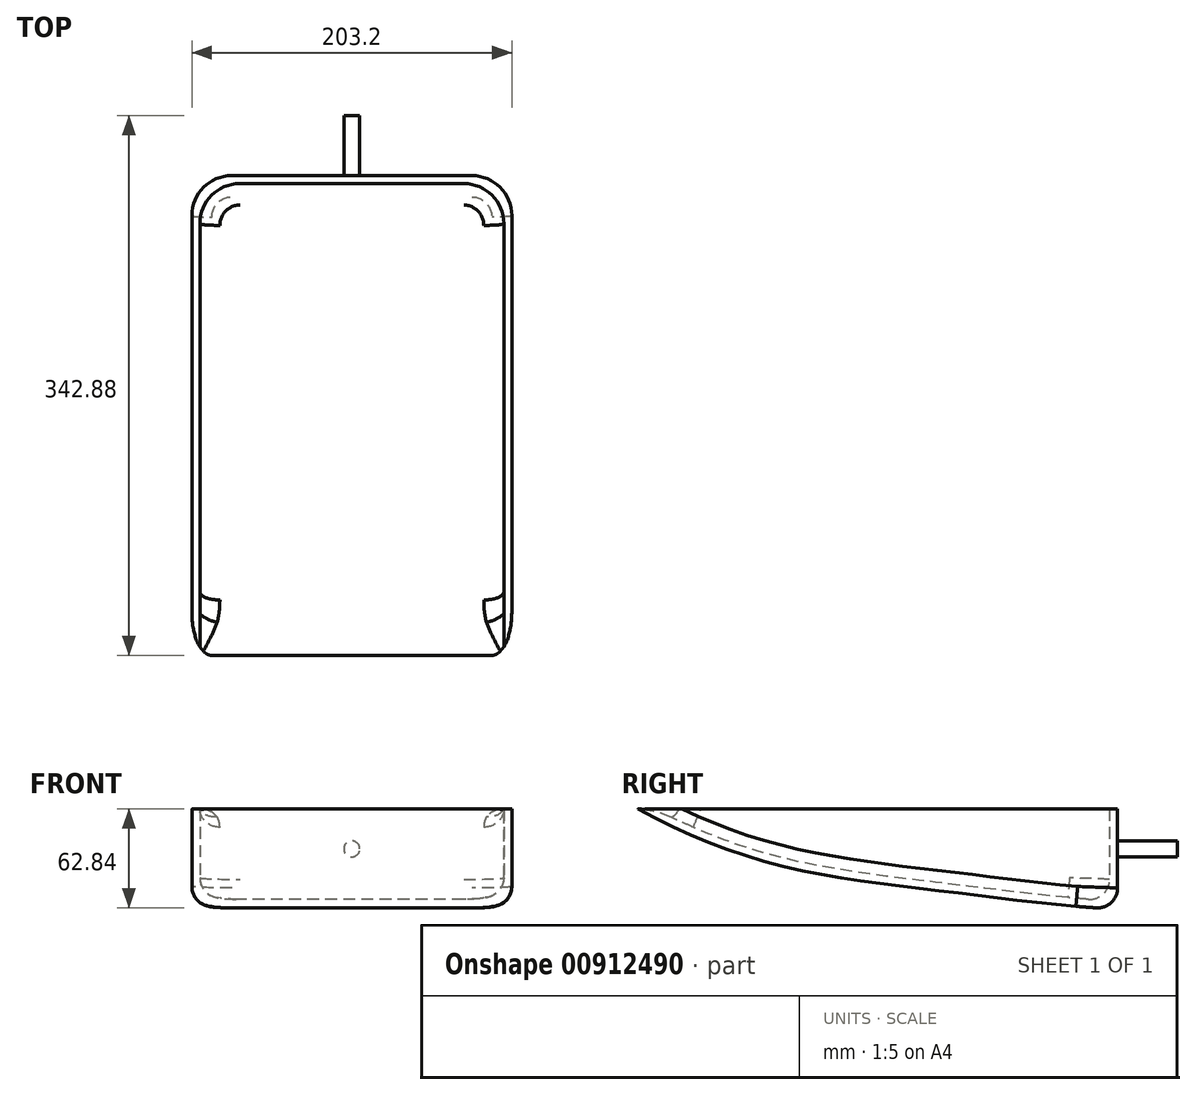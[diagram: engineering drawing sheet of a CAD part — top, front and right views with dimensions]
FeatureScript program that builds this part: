
annotation { "Feature Type Name" : "Feature", "Feature Type Description" : "" }
export const myFeature = defineFeature(function(context is Context, id is Id, definition is map)
    precondition{}
    {
        {
            var Q0;
            Q0=qCreatedBy(makeId("Right.planeOp"),FACE);
            var sketch = newSketch(context, id + "F0", { "sketchPlane" : qUnion([Q0])});
            skLineSegment(sketch, "E0", {"start": v(-153.93, 25.4) * mm, "end": v(150.87, 25.4) * mm});
            skLineSegment(sketch, "E1", {"start": v(150.87, 25.4) * mm, "end": v(150.87, -38.1) * mm});
            skFitSpline(sketch, "E2", {"points": [v(150.87, -38.1) * mm, v(48.07, -27.8) * mm, v(-62.6, -10.78) * mm, v(-153.93, 25.4) * mm], "startDerivative": vector(-306.13, 11.4) * mm, "endDerivative": vector(-268.95, 145.28) * mm});
            skLineSegment(sketch, "E3", {"start": v(131.63, 25.4) * mm, "end": v(131.63, 0) * mm, "construction": true});
            skSolve(sketch);
        }
        {
            var Q0;
            Q0=makeQuery(id+"F0.imprint","IMPRINT",FACE,{"disambiguationData":[TD([[makeQuery(id+"F0.imprint","IMPRINT",EDGE,{"derivedFrom":sQuery(id+"F0.wireOp",EDGE,"E0")}),-1.0]])]});
            extrude(context, id + "F1", {"entities" : qUnion([Q0]), "endBound" : BoundingType.SYMMETRIC, "depth" : 203.2 * mm, "offsetDistance" : 25.4 * mm});
        }
        {
            var Q0;
            Q0=makeQuery(id+"F1.opExtrude","SWEPT_FACE",FACE,{"disambiguationData":[OSD([sQuery(id+"F0.wireOp",EDGE,"E0")])]});
            shell(context, id + "F2", {"entities" : qUnion([Q0]), "thickness" : 5.08 * mm});
        }
        {
            var Q0;
            {var subQ0=sQuery(id+"F0.wireOp",EDGE,"E1");Q0=makeQuery(id+"F2.opShell","OFFSET_EDGE",EDGE,{"disambiguationData":[OSD([subQ0]),TDD([makeQuery(id+"F1.opExtrude","CAP_EDGE",EDGE,{"disambiguationData":[OSD([subQ0])],"isStart":false})])]});}
            fillet(context, id + "F3", {"entities" : qUnion([Q0]), "radius" : 25.4 * mm, "tangentPropagation" : true, "allowEdgeOverflow" : false});
        }
        {
            var Q0;
            {var subQ0=sQuery(id+"F0.wireOp",EDGE,"E1");Q0=makeQuery(id+"F2.opShell","OFFSET_EDGE",EDGE,{"disambiguationData":[OSD([subQ0]),TDD([makeQuery(id+"F1.opExtrude","CAP_EDGE",EDGE,{"disambiguationData":[OSD([subQ0])],"isStart":true})])]});}
            fillet(context, id + "F4", {"entities" : qUnion([Q0]), "radius" : 25.4 * mm, "tangentPropagation" : true, "allowEdgeOverflow" : false});
        }
        {
            var Q0;
            Q0=makeQuery(id+"F2.opShell","OFFSET_EDGE",EDGE,{"disambiguationData":[OSD([sQuery(id+"F0.wireOp",EDGE,"E0"),sQuery(id+"F0.wireOp",EDGE,"E2")])]});
            fillet(context, id + "F5", {"entities" : qUnion([Q0]), "radius" : 50.8 * mm, "tangentPropagation" : true, "allowEdgeOverflow" : false});
        }
        {
            var Q0;
            Q0=makeQuery(id+"F1.opExtrude","CAP_EDGE",EDGE,{"disambiguationData":[OSD([sQuery(id+"F0.wireOp",EDGE,"E1")])],"isStart":false});
            var Q1;
            Q1=makeQuery(id+"F1.opExtrude","CAP_EDGE",EDGE,{"disambiguationData":[OSD([sQuery(id+"F0.wireOp",EDGE,"E1")])],"isStart":true});
            fillet(context, id + "F6", {"entities" : qUnion([Q0, Q1]), "radius" : 25.4 * mm, "tangentPropagation" : true, "allowEdgeOverflow" : false});
        }
        {
            var Q0;
            Q0=makeQuery(id+"F6.opFillet","BLEND_EDGE",EDGE,{"blendedFrom":[makeQuery(id+"F1.opExtrude","CAP_EDGE",EDGE,{"disambiguationData":[OSD([sQuery(id+"F0.wireOp",EDGE,"E1")])],"isStart":false}),makeQuery(id+"F1.opExtrude","SWEPT_FACE",FACE,{"disambiguationData":[OSD([sQuery(id+"F0.wireOp",EDGE,"E2")])]})],"blendedInto":[makeQuery(id+"F1.opExtrude","SWEPT_FACE",FACE,{"disambiguationData":[OSD([sQuery(id+"F0.wireOp",EDGE,"E2")])]})]});
            fillet(context, id + "F7", {"entities" : qUnion([Q0]), "radius" : 12.7 * mm, "tangentPropagation" : true, "allowEdgeOverflow" : false});
        }
        {
            var Q0;
            Q0=makeQuery(id+"F1.opExtrude","SWEPT_FACE",FACE,{"disambiguationData":[OSD([sQuery(id+"F0.wireOp",EDGE,"E1")])]});
            var sketch = newSketch(context, id + "F8", { "sketchPlane" : qUnion([Q0])});
            skCircle(sketch, "E4", {"center": v(0, 0) * mm, "radius": 5.08 * mm});
            skSolve(sketch);
        }
        {
            var Q0;
            Q0=makeQuery(id+"F8.imprint","IMPRINT",FACE,{"disambiguationData":[TD([[makeQuery(id+"F8.imprint","IMPRINT",EDGE,{"derivedFrom":sQuery(id+"F8.wireOp",EDGE,"E4")}),1.0]])]});
            extrude(context, id + "F9", {"entities" : qUnion([Q0]), "operationType" : NewBodyOperationType.ADD, "depth" : 38.1 * mm, "offsetDistance" : 25.4 * mm});
        }
        {
            var Q0;
            {var subQ0=sQuery(id+"F0.wireOp",EDGE,"E2");Q0=makeQuery(id+"F2.opShell","OFFSET_EDGE",EDGE,{"disambiguationData":[OSD([subQ0]),TDD([makeQuery(id+"F1.opExtrude","CAP_EDGE",EDGE,{"disambiguationData":[OSD([subQ0])],"isStart":true})])]});}
            fillet(context, id + "F10", {"entities" : qUnion([Q0]), "radius" : 12.7 * mm, "tangentPropagation" : true, "allowEdgeOverflow" : false});
        }
    });
